# Revit family: 264a7878-a7e8-4eff-8c9d-0808891fdd87
name_source: partatom
category: Pipe Fittings
revit_build: Autodesk Revit 2016 (Build: 20161004_0715(x64)
units: mm (PartAtom-declared; Revit-internal decimal feet)

## family parameters
Always vertical = Yes
Cut with Voids When Loaded = No
OmniClass Number = 23.60.30.11.14
OmniClass Title = Pipework Fittings
Part Type = Union
Round Connector Dimension = Use Radius
Shared = No
Work Plane-Based = No

## types (1)
- Standard
    04 CSI = 22 00 00
    95 CSI = 15100
    Assembly Code = D2090800
    CADworks URL = http://www.CADworks.net
    Compression Liner Material = Rubber - Schott
    Coupling Band Material = Steel - Schott - Stainless
    Description = 10 Foot Length
    K Coefficient Table = Regular 45, 90 and 180 Elbow
    Lookup Table Name = Pipe_Length-Schott-10_FT-6501
    Loss Method = Not Defined
    Manufacturer = SCHOTT
    Model = 6501-1500, 6501-2000, 6501-3000, 6501-4000, 6501-6000
    Nominal Length = 10' - 0"
    Pipe Material = Glass - Schott - Borosilicate
    Product URL = http://www.us.schott.com
    Seal Ring Material = Teflon - Schott
    Series = Kimax
    Subcategory = Pipe
    URL = http://www.us.schott.com

## geometry (parser evidence)
native form markers: Blend x3, Revolve x2, Sweep x6
no freeform markers — native parametric forms only
